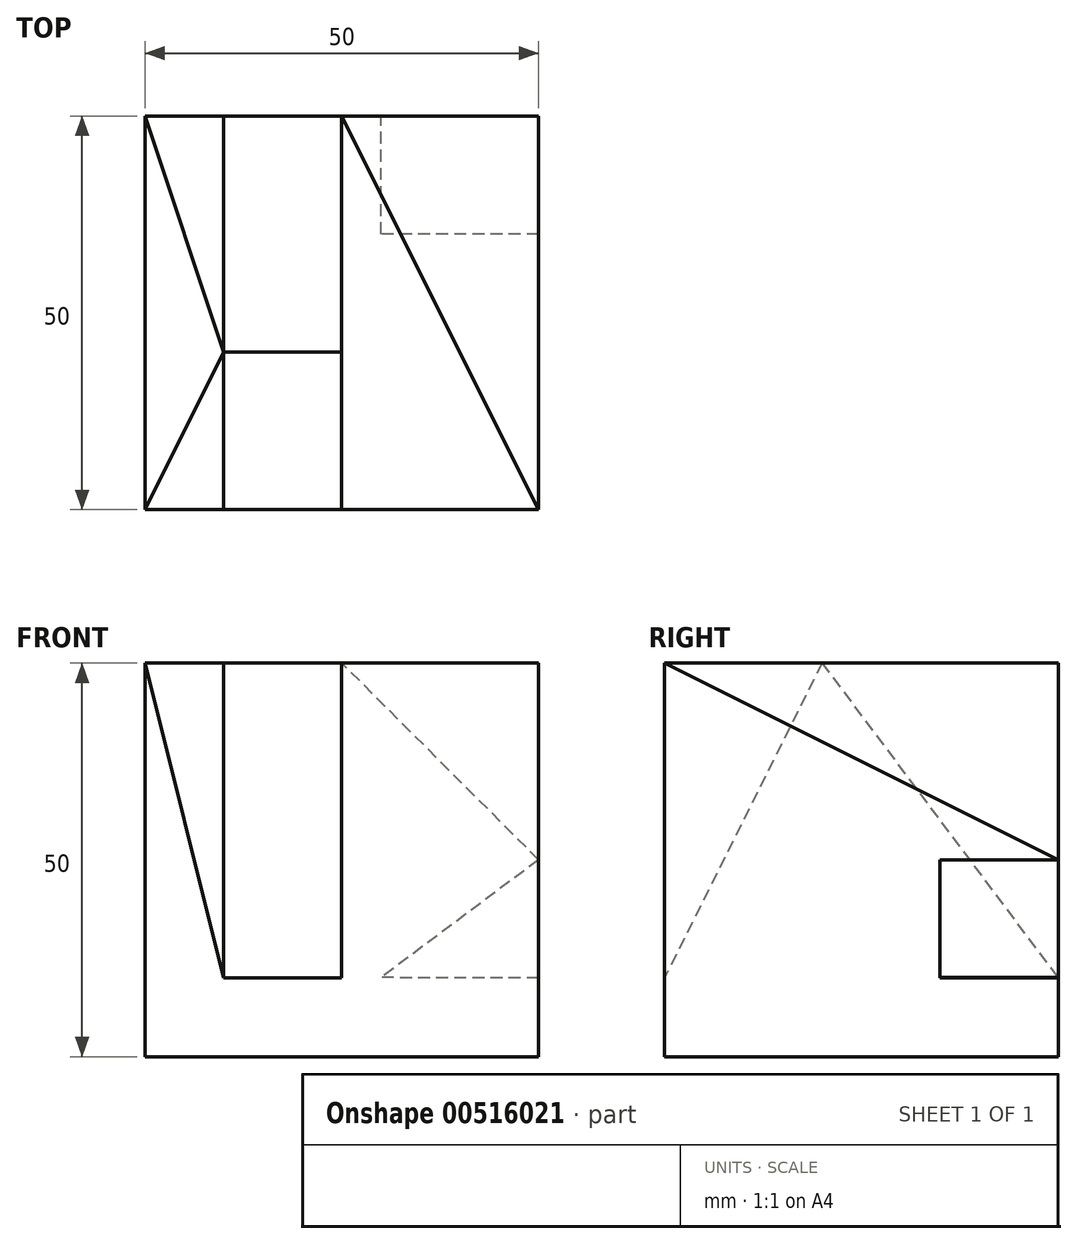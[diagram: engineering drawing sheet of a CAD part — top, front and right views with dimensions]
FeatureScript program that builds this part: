
annotation { "Feature Type Name" : "Feature", "Feature Type Description" : "" }
export const myFeature = defineFeature(function(context is Context, id is Id, definition is map)
    precondition{}
    {
        {
            var Q0;
            Q0=qCreatedBy(makeId("Top.planeOp"),FACE);
            var sketch = newSketch(context, id + "F0", { "sketchPlane" : qUnion([Q0])});
            skLineSegment(sketch, "E0.bottom", {"start": v(0, 0) * mm, "end": v(50, 0) * mm});
            skLineSegment(sketch, "E0.top", {"start": v(0, 50) * mm, "end": v(50, 50) * mm});
            skLineSegment(sketch, "E0.left", {"start": v(0, 0) * mm, "end": v(0, 50) * mm});
            skLineSegment(sketch, "E0.right", {"start": v(50, 0) * mm, "end": v(50, 50) * mm});
            skSolve(sketch);
        }
        {
            var Q0;
            Q0 = qSketchRegion(id + "F0", true);
            extrude(context, id + "F1", {"entities" : qUnion([Q0]), "depth" : 50 * mm, "offsetDistance" : 25 * mm});
        }
        {
            var Q0;
            Q0=makeQuery(id+"F1.opExtrude","CAP_FACE",FACE,{"disambiguationData":[OSD([sQuery(id+"F0.wireOp",EDGE,"E0.bottom"),sQuery(id+"F0.wireOp",EDGE,"E0.top"),sQuery(id+"F0.wireOp",EDGE,"E0.left"),sQuery(id+"F0.wireOp",EDGE,"E0.right")])],"isStart":false});
            var sketch = newSketch(context, id + "F2", { "sketchPlane" : qUnion([Q0])});
            skLineSegment(sketch, "E1", {"start": v(0, 50) * mm, "end": v(10, 20) * mm});
            skLineSegment(sketch, "E2", {"start": v(10, 20) * mm, "end": v(10, 50) * mm});
            skSolve(sketch);
        }
        {
            var Q0;
            Q0=makeQuery(id+"F1.opExtrude","SWEPT_FACE",FACE,{"disambiguationData":[OSD([sQuery(id+"F0.wireOp",EDGE,"E0.left")])]});
            var sketch = newSketch(context, id + "F3", { "sketchPlane" : qUnion([Q0])});
            skLineSegment(sketch, "E3", {"start": v(-20, 50) * mm, "end": v(-50, 10) * mm});
            skSolve(sketch);
        }
        {
            var Q0;
            {var subQ0=sQuery(id+"F2.wireOp",EDGE,"E1");Q0=makeQuery(id+"F2.imprint","IMPRINT",FACE,{"disambiguationData":[TD([[makeQuery(id+"F2.imprint","IMPRINT",EDGE,{"derivedFrom":subQ0}),1.0]])]});}
            var Q1;
            Q1=sQuery(id+"F3.wireOp",EDGE,"E3");
            sweep(context, id + "F4", {"operationType" : NewBodyOperationType.REMOVE, "profiles" : qUnion([Q0]), "path" : qUnion([Q1])});
        }
        {
            var Q0;
            Q0=makeQuery(id+"F1.opExtrude","CAP_FACE",FACE,{"disambiguationData":[OSD([sQuery(id+"F0.wireOp",EDGE,"E0.bottom"),sQuery(id+"F0.wireOp",EDGE,"E0.top"),sQuery(id+"F0.wireOp",EDGE,"E0.left"),sQuery(id+"F0.wireOp",EDGE,"E0.right")])],"isStart":false});
            var sketch = newSketch(context, id + "F5", { "sketchPlane" : qUnion([Q0])});
            skLineSegment(sketch, "E4", {"start": v(10, 20) * mm, "end": v(10, 0) * mm});
            skLineSegment(sketch, "E5", {"start": v(10, 20) * mm, "end": v(0, 0) * mm});
            skSolve(sketch);
        }
        {
            var Q0;
            Q0=makeQuery(id+"F1.opExtrude","SWEPT_FACE",FACE,{"disambiguationData":[OSD([sQuery(id+"F0.wireOp",EDGE,"E0.left")])]});
            var sketch = newSketch(context, id + "F6", { "sketchPlane" : qUnion([Q0])});
            skLineSegment(sketch, "E6", {"start": v(-20, 50) * mm, "end": v(0, 10) * mm});
            skSolve(sketch);
        }
        {
            var Q0;
            {var subQ0=sQuery(id+"F5.wireOp",EDGE,"E4");Q0=makeQuery(id+"F5.imprint","IMPRINT",FACE,{"disambiguationData":[TD([[makeQuery(id+"F5.imprint","IMPRINT",EDGE,{"derivedFrom":subQ0}),-1.0]])]});}
            var Q1;
            Q1=sQuery(id+"F6.wireOp",EDGE,"E6");
            sweep(context, id + "F7", {"operationType" : NewBodyOperationType.REMOVE, "profiles" : qUnion([Q0]), "path" : qUnion([Q1])});
        }
        {
            var Q0;
            {var subQ0=sQuery(id+"F0.wireOp",EDGE,"E0.top");var subQ3=sQuery(id+"F0.wireOp",EDGE,"E0.right");var subQ4=sQuery(id+"F0.wireOp",EDGE,"E0.bottom");var subQ5=makeQuery(id+"F1.opExtrude","CAP_FACE",FACE,{"disambiguationData":[OSD([subQ4,subQ0,sQuery(id+"F0.wireOp",EDGE,"E0.left"),subQ3])],"isStart":false});Q0=makeQuery(id+"F7.boolean.opBoolean","SPLIT",FACE,{"disambiguationData":[TD([makeQuery(id+"F1.opExtrude","SWEPT_FACE",FACE,{"disambiguationData":[OSD([subQ3])]})])],"derivedFrom":subQ5});}
            var sketch = newSketch(context, id + "F8", { "sketchPlane" : qUnion([Q0])});
            skLineSegment(sketch, "E7", {"start": v(25, 50) * mm, "end": v(50, 0) * mm});
            skSolve(sketch);
        }
        {
            var Q0;
            Q0=makeQuery(id+"F1.opExtrude","SWEPT_FACE",FACE,{"disambiguationData":[OSD([sQuery(id+"F0.wireOp",EDGE,"E0.right")])]});
            var sketch = newSketch(context, id + "F9", { "sketchPlane" : qUnion([Q0])});
            skLineSegment(sketch, "E8", {"start": v(0, 50) * mm, "end": v(50, 25) * mm});
            skSolve(sketch);
        }
        {
            var Q0;
            {var subQ0=sQuery(id+"F8.wireOp",EDGE,"E7");Q0=makeQuery(id+"F8.imprint","IMPRINT",FACE,{"disambiguationData":[TD([[makeQuery(id+"F8.imprint","IMPRINT",EDGE,{"derivedFrom":subQ0}),1.0]])]});}
            var Q1;
            Q1=sQuery(id+"F9.wireOp",EDGE,"E8");
            sweep(context, id + "F10", {"operationType" : NewBodyOperationType.REMOVE, "profiles" : qUnion([Q0]), "path" : qUnion([Q1])});
        }
        {
            var Q0;
            {var subQ0=sQuery(id+"F0.wireOp",EDGE,"E0.top");var subQ3=sQuery(id+"F0.wireOp",EDGE,"E0.right");var subQ4=sQuery(id+"F0.wireOp",EDGE,"E0.bottom");var subQ5=makeQuery(id+"F1.opExtrude","CAP_FACE",FACE,{"disambiguationData":[OSD([subQ4,subQ0,sQuery(id+"F0.wireOp",EDGE,"E0.left"),subQ3])],"isStart":false});Q0=makeQuery(id+"F7.boolean.opBoolean","SPLIT",FACE,{"disambiguationData":[TD([makeQuery(id+"F1.opExtrude","SWEPT_FACE",FACE,{"disambiguationData":[OSD([subQ3])]})])],"derivedFrom":subQ5});}
            var sketch = newSketch(context, id + "F11", { "sketchPlane" : qUnion([Q0])});
            skLineSegment(sketch, "E9", {"start": v(25, 50) * mm, "end": v(25, 0) * mm});
            skLineSegment(sketch, "E10", {"start": v(25, 20) * mm, "end": v(10, 20) * mm});
            skSolve(sketch);
        }
        {
            var Q0;
            Q0=makeQuery(id+"F1.opExtrude","SWEPT_FACE",FACE,{"disambiguationData":[OSD([sQuery(id+"F0.wireOp",EDGE,"E0.left")])]});
            var sketch = newSketch(context, id + "F12", { "sketchPlane" : qUnion([Q0])});
            skLineSegment(sketch, "E11", {"start": v(-20, 50) * mm, "end": v(0, 10) * mm});
            skSolve(sketch);
        }
        {
            var Q0;
            {var subQ3=sQuery(id+"F11.wireOp",EDGE,"E10");Q0=makeQuery(id+"F11.imprint","IMPRINT",FACE,{"disambiguationData":[TD([[makeQuery(id+"F11.imprint","IMPRINT",EDGE,{"derivedFrom":subQ3}),1.0]])]});}
            var Q1;
            Q1=sQuery(id+"F12.wireOp",EDGE,"E11");
            sweep(context, id + "F13", {"operationType" : NewBodyOperationType.REMOVE, "profiles" : qUnion([Q0]), "path" : qUnion([Q1])});
        }
        {
            var Q0;
            {var subQ0=sQuery(id+"F0.wireOp",EDGE,"E0.top");var subQ3=sQuery(id+"F0.wireOp",EDGE,"E0.right");var subQ4=sQuery(id+"F0.wireOp",EDGE,"E0.bottom");var subQ5=makeQuery(id+"F1.opExtrude","CAP_FACE",FACE,{"disambiguationData":[OSD([subQ4,subQ0,sQuery(id+"F0.wireOp",EDGE,"E0.left"),subQ3])],"isStart":false});Q0=makeQuery(id+"F7.boolean.opBoolean","SPLIT",FACE,{"disambiguationData":[TD([makeQuery(id+"F1.opExtrude","SWEPT_FACE",FACE,{"disambiguationData":[OSD([subQ3])]})])],"derivedFrom":subQ5});}
            var sketch = newSketch(context, id + "F14", { "sketchPlane" : qUnion([Q0])});
            skLineSegment(sketch, "E12", {"start": v(25, 20) * mm, "end": v(25, 50) * mm});
            skSolve(sketch);
        }
        {
            var Q0;
            Q0=makeQuery(id+"F1.opExtrude","SWEPT_FACE",FACE,{"disambiguationData":[OSD([sQuery(id+"F0.wireOp",EDGE,"E0.left")])]});
            var sketch = newSketch(context, id + "F15", { "sketchPlane" : qUnion([Q0])});
            skLineSegment(sketch, "E13", {"start": v(-20, 50) * mm, "end": v(-50, 10) * mm});
            skSolve(sketch);
        }
        {
            var Q0;
            Q0=makeQuery(id+"F14.imprint","IMPRINT",FACE,{"disambiguationData":[TD([[makeQuery(id+"F14.imprint","IMPRINT",EDGE,{"derivedFrom":sQuery(id+"F14.wireOp",EDGE,"E12")}),1.0]])]});
            var Q1;
            Q1=sQuery(id+"F15.wireOp",EDGE,"E13");
            sweep(context, id + "F16", {"operationType" : NewBodyOperationType.REMOVE, "profiles" : qUnion([Q0]), "path" : qUnion([Q1])});
        }
        {
            var Q0;
            Q0=makeQuery(id+"F1.opExtrude","SWEPT_FACE",FACE,{"disambiguationData":[OSD([sQuery(id+"F0.wireOp",EDGE,"E0.top")])]});
            var sketch = newSketch(context, id + "F17", { "sketchPlane" : qUnion([Q0])});
            skLineSegment(sketch, "E14", {"start": v(-50, 25) * mm, "end": v(-30, 10.04) * mm});
            skLineSegment(sketch, "E15", {"start": v(-50, 10) * mm, "end": v(-30, 10.04) * mm});
            skSolve(sketch);
        }
        {
            var Q0;
            {var subQ0=sQuery(id+"F17.wireOp",EDGE,"E14");Q0=makeQuery(id+"F17.imprint","IMPRINT",FACE,{"disambiguationData":[TD([[makeQuery(id+"F17.imprint","IMPRINT",EDGE,{"derivedFrom":subQ0}),-1.0]])]});}
            extrude(context, id + "F18", {"entities" : qUnion([Q0]), "operationType" : NewBodyOperationType.REMOVE, "oppositeDirection" : true, "depth" : 15 * mm, "offsetDistance" : 25 * mm});
        }
    });
